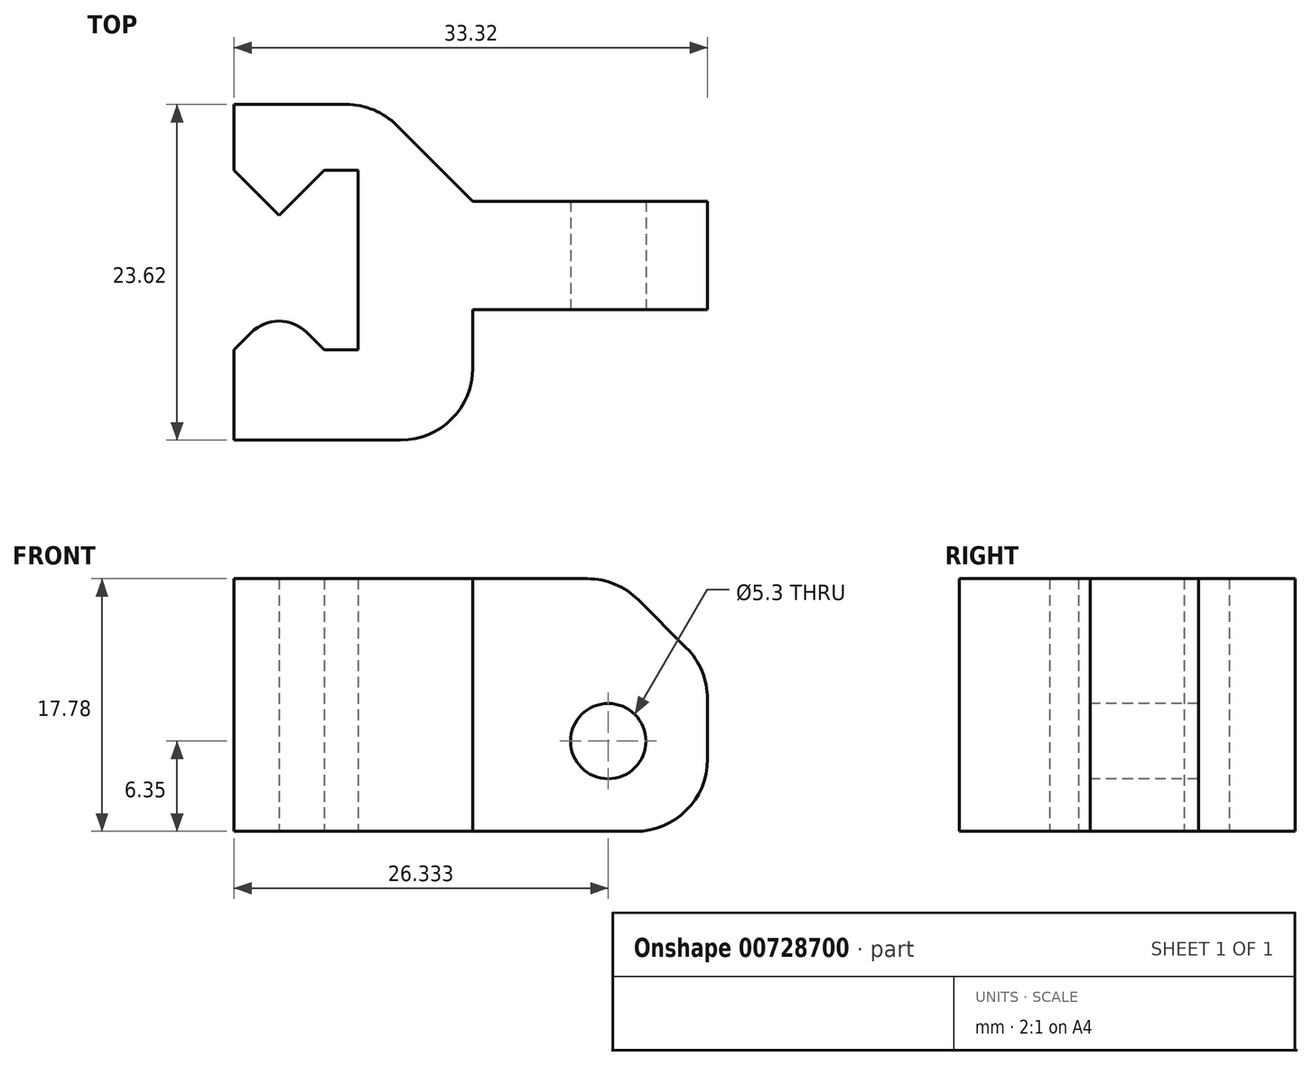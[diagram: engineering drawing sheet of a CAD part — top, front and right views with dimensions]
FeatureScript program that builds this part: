
annotation { "Feature Type Name" : "Feature", "Feature Type Description" : "" }
export const myFeature = defineFeature(function(context is Context, id is Id, definition is map)
    precondition{}
    {
        {
            var Q0;
            Q0=qCreatedBy(makeId("Top.planeOp"),FACE);
            var sketch = newSketch(context, id + "F0", { "sketchPlane" : qUnion([Q0])});
            skLineSegment(sketch, "E0", {"start": v(5.56, -11.6) * mm, "end": v(3.18, -11.6) * mm});
            skLineSegment(sketch, "E1", {"start": v(3.18, -11.6) * mm, "end": v(0, -8.43) * mm});
            skLineSegment(sketch, "E2", {"start": v(0, -8.43) * mm, "end": v(-3.18, -11.6) * mm});
            skLineSegment(sketch, "E3", {"start": v(-3.18, -11.6) * mm, "end": v(-3.18, -17.96) * mm});
            skLineSegment(sketch, "E4", {"start": v(-3.18, -17.96) * mm, "end": v(30.44, -17.96) * mm});
            skLineSegment(sketch, "E5", {"start": v(-0.4, 5.66) * mm, "end": v(6.81, 5.66) * mm});
            skLineSegment(sketch, "E6", {"start": v(6.81, 5.66) * mm, "end": v(30.44, -17.96) * mm});
            skPoint(sketch, "E7.endSnap0", {"position": v(13.63, -17.96) * mm});
            skLineSegment(sketch, "E8", {"start": v(13.63, -1.15) * mm, "end": v(13.63, -17.96) * mm});
            skLineSegment(sketch, "E9", {"start": v(5.56, -11.6) * mm, "end": v(5.56, 1.03) * mm});
            skLineSegment(sketch, "E10", {"start": v(3.18, 1.03) * mm, "end": v(5.56, 1.03) * mm});
            skLineSegment(sketch, "E11", {"start": v(3.18, 1.03) * mm, "end": v(0, -2.15) * mm});
            skLineSegment(sketch, "E12", {"start": v(0, -2.15) * mm, "end": v(-3.18, 1.03) * mm});
            skLineSegment(sketch, "E13", {"start": v(-3.18, 5.66) * mm, "end": v(-0.4, 5.66) * mm});
            skLineSegment(sketch, "E14", {"start": v(-3.18, 5.66) * mm, "end": v(-3.18, 1.03) * mm});
            skSolve(sketch);
        }
        {
            var Q0;
            Q0=makeQuery(id+"F0.imprint","IMPRINT",FACE,{"disambiguationData":[TD([[makeQuery(id+"F0.imprint","IMPRINT",EDGE,{"derivedFrom":sQuery(id+"F0.wireOp",EDGE,"ketpRVbD-6SFL-thPw-nqCE-cJDCLMVs4f7w")}),-1.0]])]});
            var Q1;
            Q1=makeQuery(id+"F0.imprint","IMPRINT",FACE,{"disambiguationData":[TD([[makeQuery(id+"F0.imprint","IMPRINT",EDGE,{"derivedFrom":sQuery(id+"F0.wireOp",EDGE,"E0")}),1.0]])]});
            extrude(context, id + "F1", {"entities" : qUnion([Q0, Q1]), "depth" : 17.78 * mm, "offsetDistance" : 25.4 * mm});
        }
        {
            var Q0;
            Q0=makeQuery(id+"F1.opExtrude","SWEPT_FACE",FACE,{"disambiguationData":[OSD([sQuery(id+"F0.wireOp",EDGE,"E8")])]});
            var sketch = newSketch(context, id + "F2", { "sketchPlane" : qUnion([Q0])});
            skLineSegment(sketch, "E15", {"start": v(-1.15, 0) * mm, "end": v(-1.15, 17.78) * mm});
            skLineSegment(sketch, "E16", {"start": v(-1.15, 17.78) * mm, "end": v(-8.77, 17.78) * mm});
            skLineSegment(sketch, "E17", {"start": v(-8.77, 17.78) * mm, "end": v(-8.77, 0) * mm});
            skLineSegment(sketch, "E18", {"start": v(-8.77, 0) * mm, "end": v(-1.15, 0) * mm});
            skSolve(sketch);
        }
        {
            var Q0;
            Q0=qSketchRegion(id+"F2",true);
            extrude(context, id + "F3", {"entities" : qUnion([Q0]), "operationType" : NewBodyOperationType.ADD, "depth" : 16.5 * mm, "offsetDistance" : 25.4 * mm});
        }
        {
            var Q0;
            Q0=makeQuery(id+"F3.opExtrude","CAP_EDGE",EDGE,{"disambiguationData":[OSD([sQuery(id+"F2.wireOp",EDGE,"iHOXsHoF-hqfp-rUCR-3NdC-NWc7uM61uAc2")])],"isStart":false});
            var Q1;
            Q1=makeQuery(id+"F3.opExtrude","CAP_EDGE",EDGE,{"disambiguationData":[OSD([sQuery(id+"F2.wireOp",EDGE,"E16")])],"isStart":false});
            chamfer(context, id + "F4", {"entities" : qUnion([Q0, Q1]), "width" : 6.35 * mm, "tangentPropagation" : true});
        }
        {
            var Q0;
            Q0=makeQuery(id+"F3.opExtrude","SWEPT_FACE",FACE,{"disambiguationData":[OSD([sQuery(id+"F2.wireOp",EDGE,"E17")])]});
            var sketch = newSketch(context, id + "F5", { "sketchPlane" : qUnion([Q0])});
            skCircle(sketch, "E19", {"center": v(23.15, 6.35) * mm, "radius": 2.65 * mm});
            skSolve(sketch);
        }
        {
            var Q0;
            Q0=qSketchRegion(id+"F5",true);
            extrude(context, id + "F6", {"entities" : qUnion([Q0]), "operationType" : NewBodyOperationType.REMOVE, "oppositeDirection" : true, "depth" : 25.4 * mm, "offsetDistance" : 25.4 * mm});
        }
        {
            var Q0;
            Q0=makeQuery(id+"F1.opExtrude","SWEPT_EDGE",EDGE,{"disambiguationData":[OSD([sQuery(id+"F0.wireOp",EDGE,"E1"),sQuery(id+"F0.wireOp",EDGE,"E2")])]});
            fillet(context, id + "F7", {"entities" : qUnion([Q0]), "radius" : 2.8 * mm, "tangentPropagation" : true, "allowEdgeOverflow" : false});
        }
        {
            var Q0;
            Q0=makeQuery(id+"F1.opExtrude","SWEPT_EDGE",EDGE,{"disambiguationData":[OSD([sQuery(id+"F0.wireOp",EDGE,"E5"),sQuery(id+"F0.wireOp",EDGE,"E6")])]});
            fillet(context, id + "F8", {"entities" : qUnion([Q0]), "radius" : 5.08 * mm, "tangentPropagation" : true, "allowEdgeOverflow" : false});
        }
        {
            var Q0;
            Q0=makeQuery(id+"F3.opExtrude","CAP_EDGE",EDGE,{"disambiguationData":[OSD([sQuery(id+"F2.wireOp",EDGE,"E18")])],"isStart":false});
            fillet(context, id + "F9", {"entities" : qUnion([Q0]), "radius" : 5.08 * mm, "tangentPropagation" : true, "allowEdgeOverflow" : false});
        }
        {
            var Q0;
            Q0=makeQuery(id+"F1.opExtrude","SWEPT_EDGE",EDGE,{"disambiguationData":[OSD([sQuery(id+"F0.wireOp",EDGE,"E4"),sQuery(id+"F0.wireOp",EDGE,"E8")])]});
            fillet(context, id + "F10", {"entities" : qUnion([Q0]), "radius" : 5.08 * mm, "tangentPropagation" : true, "allowEdgeOverflow" : false});
        }
        {
            var Q0;
            {var subQ0=sQuery(id+"F2.wireOp",EDGE,"E16");Q0=makeQuery(id+"F4.opChamfer","BLEND_EDGE",EDGE,{"blendedFrom":[makeQuery(id+"F3.opExtrude","CAP_EDGE",EDGE,{"disambiguationData":[OSD([subQ0])],"isStart":false}),makeQuery(id+"F3.opExtrude","CAP_FACE",FACE,{"disambiguationData":[OSD([sQuery(id+"F2.wireOp",EDGE,"E15"),subQ0,sQuery(id+"F2.wireOp",EDGE,"E17"),sQuery(id+"F2.wireOp",EDGE,"E18")])],"isStart":false})],"blendedInto":[makeQuery(id+"F3.opExtrude","CAP_FACE",FACE,{"disambiguationData":[OSD([sQuery(id+"F2.wireOp",EDGE,"E15"),subQ0,sQuery(id+"F2.wireOp",EDGE,"E17"),sQuery(id+"F2.wireOp",EDGE,"E18")])],"isStart":false})]});}
            var Q1;
            {var subQ0=sQuery(id+"F2.wireOp",EDGE,"E16");Q1=makeQuery(id+"F4.opChamfer","BLEND_EDGE",EDGE,{"blendedFrom":[makeQuery(id+"F3.opExtrude","CAP_EDGE",EDGE,{"disambiguationData":[OSD([subQ0])],"isStart":false}),makeQuery(id+"F3.boolean.opBoolean","MERGE",FACE,{"derivedFrom":[makeQuery(id+"F1.opExtrude","CAP_FACE",FACE,{"disambiguationData":[OSD([sQuery(id+"F0.wireOp",EDGE,"E0"),sQuery(id+"F0.wireOp",EDGE,"E1"),sQuery(id+"F0.wireOp",EDGE,"E2"),sQuery(id+"F0.wireOp",EDGE,"E3"),sQuery(id+"F0.wireOp",EDGE,"E4"),sQuery(id+"F0.wireOp",EDGE,"E5"),sQuery(id+"F0.wireOp",EDGE,"E6"),sQuery(id+"F0.wireOp",EDGE,"E8"),sQuery(id+"F0.wireOp",EDGE,"E9"),sQuery(id+"F0.wireOp",EDGE,"E10"),sQuery(id+"F0.wireOp",EDGE,"E11"),sQuery(id+"F0.wireOp",EDGE,"E12"),sQuery(id+"F0.wireOp",EDGE,"E13"),sQuery(id+"F0.wireOp",EDGE,"E14")])],"isStart":false}),makeQuery(id+"F3.opExtrude","SWEPT_FACE",FACE,{"disambiguationData":[OSD([subQ0])]})]})],"blendedInto":[makeQuery(id+"F3.boolean.opBoolean","MERGE",FACE,{"derivedFrom":[makeQuery(id+"F1.opExtrude","CAP_FACE",FACE,{"disambiguationData":[OSD([sQuery(id+"F0.wireOp",EDGE,"E0"),sQuery(id+"F0.wireOp",EDGE,"E1"),sQuery(id+"F0.wireOp",EDGE,"E2"),sQuery(id+"F0.wireOp",EDGE,"E3"),sQuery(id+"F0.wireOp",EDGE,"E4"),sQuery(id+"F0.wireOp",EDGE,"E5"),sQuery(id+"F0.wireOp",EDGE,"E6"),sQuery(id+"F0.wireOp",EDGE,"E8"),sQuery(id+"F0.wireOp",EDGE,"E9"),sQuery(id+"F0.wireOp",EDGE,"E10"),sQuery(id+"F0.wireOp",EDGE,"E11"),sQuery(id+"F0.wireOp",EDGE,"E12"),sQuery(id+"F0.wireOp",EDGE,"E13"),sQuery(id+"F0.wireOp",EDGE,"E14")])],"isStart":false}),makeQuery(id+"F3.opExtrude","SWEPT_FACE",FACE,{"disambiguationData":[OSD([subQ0])]})]})]});}
            fillet(context, id + "F11", {"entities" : qUnion([Q0, Q1]), "radius" : 5.08 * mm, "tangentPropagation" : true, "allowEdgeOverflow" : false});
        }
    });
